# Revit family: Zumtobel TECTON 2 continuous row element RESCLITE PRO
name_source: partatom
category: Lighting Fixtures
units: mm (PartAtom-declared; Revit-internal decimal feet)

## family parameters
Cut with Voids When Loaded = Yes
Host = Face
Light Source = No
Maintain Annotation Orientation = No
Part Type = Normal
Room Calculation Point = Yes
Round Connector Dimension = Use Diameter
Shared = Yes

## types (47) — shared parameters
Assembly Code = Pr_70_70_48_74
Black = No
Description = Emergency Lighting Luminaires
Export Type to IFC As = IfcLightFixtureType
Lamp = LED
Luminaire Height = 44 mm  [stored 0.144357 ft]
Luminaire Length = 250 mm  [stored 0.82021 ft]
Luminaire Width = 60 mm  [stored 0.19685 ft]
Manufacturer = Zumtobel Lighting
SELECT Colour = SELECT Colour
SELECT Radiation angle = SELECT Radiation angle
Type Black = Zumtobel-Parts-TECTON 2-RESCLITE PRO-Housing : Black
Type Housing = Zumtobel-Parts-TECTON 2-RESCLITE PRO-Housing : White
Type IFC Predefined Type = SECURITYLIGHTING
Type Image = ZS_RES_F_PRO_TECTON-II_ECx_ESC_WH.jpg
Type White = Zumtobel-Parts-TECTON 2-RESCLITE PRO-Housing : White
URL = https://www.zumtobel.com
White = Yes
zero-valued in all types: Default Elevation

## per-type parameters (varying)
| type | Antipanic | Apparent Load | Escape | Escape 90 | Model | Power Factor | Spot | Type Light Source | Wattage |
| RESPRO TEC2 ANT E1D WH | Yes | 7 VA | No | No | 42191036 | 0.7 | No | Zumtobel-Light Source-TECTON 2-RESCLITE PRO : 42191036 | 5 W |
| RESPRO TEC2 ANT E3D WH | Yes | 7 VA | No | No | 42191423 | 0.7 | No | Zumtobel-Light Source-TECTON 2-RESCLITE PRO : 42191423 | 5 W |
| RESPRO TEC2 ESC E1D WH | No | 7 VA | Yes | No | 42191332 | 0.7 | No | Zumtobel-Light Source-TECTON 2-RESCLITE PRO : 42191332 | 5 W |
| RESPRO TEC2 ESC E3D WH | No | 7 VA | Yes | No | 42191331 | 0.7 | No | Zumtobel-Light Source-TECTON 2-RESCLITE PRO : 42191331 | 5 W |
| RESPRO TEC2 ESC90 E3D WH | No | 7 VA | No | Yes | 42191393 | 0.7 | No | Zumtobel-Light Source-TECTON 2-RESCLITE PRO : 42191393 | 5 W |
| RESPRO TEC2 SPOT E3D WH | No | 7 VA | No | No | 42191394 | 0.7 | Yes | Zumtobel-Light Source-TECTON 2-RESCLITE PRO : 42191394 | 5 W |
| <RESPRO TEC2 ESC HP E1D WH | No | 10 VA | Yes | No | 42191422 | 0.84 | No | Zumtobel-Light Source-TECTON 2-RESCLITE PRO : 42191422 | 8 W |
| <RESPRO TEC2 SPOT HP E1D WH | No | 10 VA | No | No | 42191390 | 0.84 | Yes | Zumtobel-Light Source-TECTON 2-RESCLITE PRO : 42191390 | 8 W |
| RESPRO TEC2 ESC90 HP E1D WH | No | 10 VA | No | Yes | 42191389 | 0.84 | No | Zumtobel-Light Source-TECTON 2-RESCLITE PRO : 42191389 | 8 W |
| RESPRO TEC2 ANT HC E1D WH | Yes | 8 VA | No | No | 42191391 | 0.79 | No | Zumtobel-Light Source-TECTON 2-RESCLITE PRO : 42191391 | 7 W |
| RESPRO TEC2 ESC HC E1D WH | No | 8 VA | Yes | No | 42191392 | 0.79 | No | Zumtobel-Light Source-TECTON 2-RESCLITE PRO : 42191392 | 7 W |
| <RESPRO TEC2 SPOT ECC WH | No | 6 VA | No | No | 42191400 | 0.65 | Yes | Zumtobel-Light Source-TECTON 2-RESCLITE PRO : 42191400 | 4 W |
| RESPRO TEC2 ANT ECC WH | Yes | 6 VA | No | No | 42191424 | 0.65 | No | Zumtobel-Light Source-TECTON 2-RESCLITE PRO : 42191424 | 4 W |
| RESPRO TEC2 ANT ECD WH | Yes | 6 VA | No | No | 42191333 | 0.66 | No | Zumtobel-Light Source-TECTON 2-RESCLITE PRO : 42191333 | 4 W |
| RESPRO TEC2 ANT ECP WH | Yes | 6 VA | No | No | 42191037 | 0.65 | No | Zumtobel-Light Source-TECTON 2-RESCLITE PRO : 42191037 | 4 W |
| RESPRO TEC2 ANT ELP WH | Yes | 5 VA | No | No | 42191425 | 0.65 | No | Zumtobel-Light Source-TECTON 2-RESCLITE PRO : 42191425 | 3 W |
| RESPRO TEC2 ESC ECC WH | No | 6 VA | Yes | No | 42191401 | 0.65 | No | Zumtobel-Light Source-TECTON 2-RESCLITE PRO : 42191401 | 4 W |
| RESPRO TEC2 ESC ECD WH | No | 6 VA | Yes | No | 42191408 | 0.66 | No | Zumtobel-Light Source-TECTON 2-RESCLITE PRO : 42191408 | 4 W |
| RESPRO TEC2 ESC ECP WH | No | 6 VA | Yes | No | 42191334 | 0.65 | No | Zumtobel-Light Source-TECTON 2-RESCLITE PRO : 42191334 | 4 W |
| RESPRO TEC2 ESC ELP WH | No | 5 VA | Yes | No | 42191388 | 0.65 | No | Zumtobel-Light Source-TECTON 2-RESCLITE PRO : 42191388 | 3 W |
| RESPRO TEC2 ESC90 ECC WH | No | 6 VA | No | Yes | 42191399 | 0.65 | No | Zumtobel-Light Source-TECTON 2-RESCLITE PRO : 42191399 | 4 W |
| RESPRO TEC2 ESC90 ECD WH | No | 6 VA | No | Yes | 42191409 | 0.66 | No | Zumtobel-Light Source-TECTON 2-RESCLITE PRO : 42191409 | 4 W |
| RESPRO TEC2 ESC90 ECP WH | No | 6 VA | No | Yes | 42191416 | 0.65 | No | Zumtobel-Light Source-TECTON 2-RESCLITE PRO : 42191416 | 4 W |
| RESPRO TEC2 ESC90 ELP WH | No | 5 VA | No | Yes | 42191387 | 0.65 | No | Zumtobel-Light Source-TECTON 2-RESCLITE PRO : 42191387 | 3 W |
| RESPRO TEC2 SPOT ECD WH | No | 6 VA | No | No | 42191410 | 0.66 | Yes | Zumtobel-Light Source-TECTON 2-RESCLITE PRO : 42191410 | 4 W |
| RESPRO TEC2 SPOT ECP WH | No | 6 VA | No | No | 42191417 | 0.65 | Yes | Zumtobel-Light Source-TECTON 2-RESCLITE PRO : 42191417 | 4 W |
| RESPRO TEC2 SPOT ELP WH | No | 5 VA | No | No | 42191386 | 0.65 | Yes | Zumtobel-Light Source-TECTON 2-RESCLITE PRO : 42191386 | 3 W |
| <RESPRO TEC2 ESC HP ECP WH | No | 9 VA | Yes | No | 42191381 | 0.8 | No | Zumtobel-Light Source-TECTON 2-RESCLITE PRO : 42191381 | 8 W |
| RESPRO TEC2 ANT HP ECC WH | Yes | 9 VA | No | No | 42191406 | 0.81 | No | Zumtobel-Light Source-TECTON 2-RESCLITE PRO : 42191406 | 7 W |
| RESPRO TEC2 ANT HP ECD WH | Yes | 9 VA | No | No | 42191330 | 0.81 | No | Zumtobel-Light Source-TECTON 2-RESCLITE PRO : 42191330 | 7 W |
| RESPRO TEC2 ANT HP ECP WH | Yes | 9 VA | No | No | 42191329 | 0.81 | No | Zumtobel-Light Source-TECTON 2-RESCLITE PRO : 42191329 | 8 W |
| RESPRO TEC2 ESC HP ECC WH | No | 9 VA | Yes | No | 42191407 | 0.81 | No | Zumtobel-Light Source-TECTON 2-RESCLITE PRO : 42191407 | 7 W |
| RESPRO TEC2 ESC HP ECD WH | No | 9 VA | Yes | No | 42191415 | 0.81 | No | Zumtobel-Light Source-TECTON 2-RESCLITE PRO : 42191415 | 7 W |
| RESPRO TEC2 ESC90 HP ECC WH | No | 9 VA | No | Yes | 42191404 | 0.81 | No | Zumtobel-Light Source-TECTON 2-RESCLITE PRO : 42191404 | 7 W |
| RESPRO TEC2 ESC90 HP ECD WH | No | 9 VA | No | Yes | 42191413 | 0.81 | No | Zumtobel-Light Source-TECTON 2-RESCLITE PRO : 42191413 | 7 W |
| RESPRO TEC2 ESC90 HP ECP WH | No | 9 VA | No | Yes | 42191420 | 0.8 | No | Zumtobel-Light Source-TECTON 2-RESCLITE PRO : 42191420 | 8 W |
| RESPRO TEC2 SPOT HP ECC WH | No | 9 VA | No | No | 42191405 | 0.81 | Yes | Zumtobel-Light Source-TECTON 2-RESCLITE PRO : 42191405 | 7 W |
| RESPRO TEC2 SPOT HP ECD WH | No | 9 VA | No | No | 42191414 | 0.81 | Yes | Zumtobel-Light Source-TECTON 2-RESCLITE PRO : 42191414 | 7 W |
| RESPRO TEC2 SPOT HP ECP WH | No | 9 VA | No | No | 42191421 | 0.8 | Yes | Zumtobel-Light Source-TECTON 2-RESCLITE PRO : 42191421 | 8 W |
| RESPRO TEC2 ANT HC ECC WH | Yes | 6 VA | No | No | 42191402 | 0.69 | No | Zumtobel-Light Source-TECTON 2-RESCLITE PRO : 42191402 | 4 W |
| RESPRO TEC2 ANT HC ECD WH | Yes | 6 VA | No | No | 42191411 | 0.7 | No | Zumtobel-Light Source-TECTON 2-RESCLITE PRO : 42191411 | 5 W |
| RESPRO TEC2 ANT HC ECP WH | Yes | 6 VA | No | No | 42191418 | 0.7 | No | Zumtobel-Light Source-TECTON 2-RESCLITE PRO : 42191418 | 5 W |
| RESPRO TEC2 ANT HC ELP WH | Yes | 6 VA | No | No | 42191385 | 0.65 | No | Zumtobel-Light Source-TECTON 2-RESCLITE PRO : 42191385 | 4 W |
| RESPRO TEC2 ESC HC ECC WH | No | 6 VA | Yes | No | 42191403 | 0.69 | No | Zumtobel-Light Source-TECTON 2-RESCLITE PRO : 42191403 | 4 W |
| RESPRO TEC2 ESC HC ECD WH | No | 6 VA | Yes | No | 42191412 | 0.7 | No | Zumtobel-Light Source-TECTON 2-RESCLITE PRO : 42191412 | 5 W |
| RESPRO TEC2 ESC HC ECP WH | No | 6 VA | Yes | No | 42191419 | 0.7 | No | Zumtobel-Light Source-TECTON 2-RESCLITE PRO : 42191419 | 5 W |
| RESPRO TEC2 ESC HC ELP WH | No | 6 VA | Yes | No | 42191384 | 0.65 | No | Zumtobel-Light Source-TECTON 2-RESCLITE PRO : 42191384 | 4 W |

note: [stored X ft] marks values corroborated as IEEE doubles in the binary element streams (Revit-internal decimal feet)

## geometry (parser evidence)
native form markers: Sweep x6
no freeform markers — native parametric forms only
